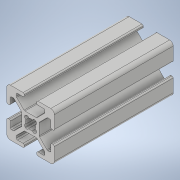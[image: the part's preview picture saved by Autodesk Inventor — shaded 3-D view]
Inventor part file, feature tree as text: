
AUTODESK INVENTOR PART (.ipt)
format: ipt  version: 2022 (Build 260153000, 153)  size: 240,640 bytes
history: native  units: mm
features: extrude x1, sketch x1
ambient origin geometry x8: Origin, YZ Plane, XZ Plane, XY Plane, X Axis, Y Axis, Z Axis, Center Point
bodies: Solid1 (feature_tree)
feature tree (2):
  extrude  "Extrusion1"  [1 undecoded]
  sketch  "Sketch_1"  dims[d0=50.0mm d1=0.0mm]
note: 1 required parameter value undecoded (feature->parameter linkage not recoverable at this tier; creation-order binding heuristic only, values carry confidence <= 0.55)
